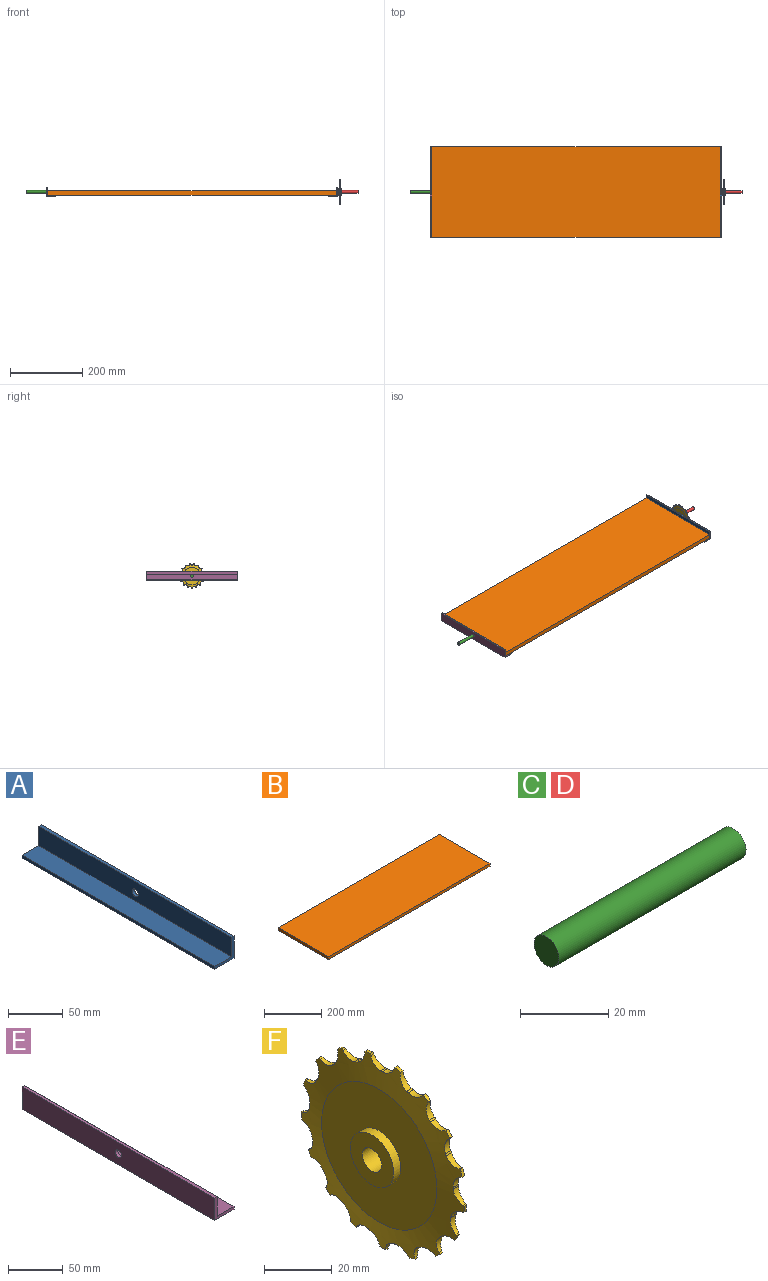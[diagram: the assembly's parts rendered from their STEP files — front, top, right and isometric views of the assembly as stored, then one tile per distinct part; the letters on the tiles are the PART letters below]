
ASSEMBLY  parts=6 mates=5
PART A: 9 faces, bbox 25x250x25 mm
  f0: plane 250x25mm, normal (0,0,-1), area 6250mm2, adj f1,f5,f6,f7
  f1: plane 250x25mm, normal (1,0,0), area 6199.7mm2, adj f0,f2,f6,f7,f8
  f2: plane 250x3.2mm, normal (0,0,1), area 800mm2, adj f1,f3,f6,f7
  f3: plane 250x21.8mm, normal (-1,0,0), area 5399.7mm2, adj f2,f4,f6,f7,f8
  f4: plane 250x21.8mm, normal (0,0,1), area 5450mm2, adj f3,f5,f6,f7
  f5: plane 250x3.2mm, normal (-1,0,0), area 800mm2, adj f0,f4,f6,f7
  f6: plane 25x25mm, normal (0,-1,0), area 149.8mm2, adj f0,f1,f2,f3,f4,f5
  f7: plane 25x25mm, normal (0,1,0), area 149.8mm2, adj f0,f1,f2,f3,f4,f5
  f8: cylinder r=4mm len=8mm, axis (1,0,0), area 80.4mm2, adj f1,f3
PART B: 6 faces, bbox 800x250x12 mm
  f0: plane 800x12mm, normal (0,1,0), area 9600mm2, adj f1,f3,f4,f5
  f1: plane 250x12mm, normal (-1,0,0), area 3000mm2, adj f0,f2,f4,f5
  f2: plane 800x12mm, normal (0,-1,0), area 9600mm2, adj f1,f3,f4,f5
  f3: plane 250x12mm, normal (1,0,0), area 3000mm2, adj f0,f2,f4,f5
  f4: plane 800x250mm, normal (0,0,1), area 200000mm2, adj f0,f1,f2,f3
  f5: plane 800x250mm, normal (0,0,-1), area 200000mm2, adj f0,f1,f2,f3
PART C: 3 faces, bbox 60x8x8 mm
  f0: cylinder r=4mm len=60mm, axis (-1,0,0), area 1508mm2, adj f1,f2
  f1: plane 8x8mm, normal (1,0,0), area 50.3mm2, adj f0
  f2: plane 8x8mm, normal (-1,0,0), area 50.3mm2, adj f0
PART D: same geometry as C
PART E: 11 faces, bbox 25x250x25 mm
  f0: plane 250x21.8mm, normal (0,0,1), area 5410.7mm2, adj f1,f5,f6,f7,f9,f10
  f1: plane 250x21.8mm, normal (1,0,0), area 5399.7mm2, adj f0,f2,f6,f7,f8
  f2: plane 250x3.2mm, normal (0,0,1), area 800mm2, adj f1,f3,f6,f7
  f3: plane 250x25mm, normal (-1,0,0), area 6199.7mm2, adj f2,f4,f6,f7,f8
  f4: plane 250x25mm, normal (0,0,-1), area 6210.7mm2, adj f3,f5,f6,f7,f9,f10
  f5: plane 250x3.2mm, normal (1,0,0), area 800mm2, adj f0,f4,f6,f7
  f6: plane 25x25mm, normal (0,-1,0), area 149.8mm2, adj f0,f1,f2,f3,f4,f5
  f7: plane 25x25mm, normal (0,1,0), area 149.8mm2, adj f0,f1,f2,f3,f4,f5
  f8: cylinder r=4mm len=8mm, axis (1,0,0), area 80.4mm2, adj f1,f3
  f9: cylinder r=2.5mm len=5mm, axis (0,0,1), area 50.3mm2, adj f0,f4
  f10: cylinder r=2.5mm len=5mm, axis (0,0,1), area 50.3mm2, adj f0,f4
PART F: 111 faces, bbox 10x68x68 mm
  f0: cylinder r=34mm len=2.49mm, axis (1,0,0), area 2.5mm2, adj f1,f97,f98,f110
  f1: plane 1.16x0.54mm, normal (0,1,-0.02), area 0.6mm2, adj f0,f2,f97,f98
  f2: cylinder r=4.75mm len=4.54mm, axis (1,0,0), area 10.7mm2, adj f1,f3,f97,f98
  f3: cylinder r=30mm len=2.2mm, axis (1,0,0), area 1.3mm2, adj f2,f4,f97,f98
  f4: cylinder r=4.75mm len=5.34mm, axis (1,0,0), area 10.7mm2, adj f3,f5,f97,f98
  f5: plane 1.16x0.41mm, normal (0,-0.75,0.66), area 0.6mm2, adj f4,f6,f97,f98
  f6: cylinder r=34mm len=2.15mm, axis (1,0,0), area 2.5mm2, adj f5,f7,f97,f98
  f7: plane 1.16x0.5mm, normal (0,0.92,-0.38), area 0.6mm2, adj f6,f8,f97,f98
  f8: cylinder r=4.75mm len=5.35mm, axis (1,0,0), area 10.7mm2, adj f7,f9,f97,f98
  f9: cylinder r=30mm len=2.2mm, axis (1,0,0), area 1.3mm2, adj f8,f10,f97,f98
  f10: cylinder r=4.75mm len=5.44mm, axis (1,0,0), area 10.7mm2, adj f9,f11,f97,f98
  f11: plane 1.16x0.48mm, normal (0,-0.46,0.89), area 0.6mm2, adj f10,f12,f97,f98
  f12: cylinder r=34mm len=2.02mm, axis (1,0,0), area 2.5mm2, adj f11,f13,f97,f98
  f13: plane 1.16x0.39mm, normal (0,0.73,-0.69), area 0.6mm2, adj f12,f14,f97,f98
  f14: cylinder r=4.75mm len=5.43mm, axis (1,0,0), area 10.7mm2, adj f13,f15,f97,f98
  f15: cylinder r=30mm len=2.2mm, axis (1,0,0), area 1.3mm2, adj f14,f16,f97,f98
  f16: cylinder r=4.75mm len=4.81mm, axis (1,0,0), area 10.7mm2, adj f15,f17,f97,f98
  f17: plane 1.16x0.54mm, normal (0,-0.11,0.99), area 0.6mm2, adj f16,f18,f97,f98
  f18: cylinder r=34mm len=2.43mm, axis (1,0,0), area 2.5mm2, adj f17,f19,f97,f98
  f19: plane 1.16x0.49mm, normal (0,0.43,-0.9), area 0.6mm2, adj f18,f20,f97,f98
  f20: cylinder r=4.75mm len=4.78mm, axis (1,0,0), area 10.7mm2, adj f19,f21,f97,f98
  f21: cylinder r=30mm len=2.2mm, axis (1,0,0), area 1.3mm2, adj f20,f22,f97,f98
  f22: cylinder r=4.75mm len=4.2mm, axis (1,0,0), area 10.7mm2, adj f21,f23,f97,f98
  f23: plane 1.16x0.52mm, normal (0,0.25,0.97), area 0.6mm2, adj f22,f24,f97,f98
  f24: cylinder r=34mm len=2.52mm, axis (1,0,0), area 2.5mm2, adj f23,f25,f97,f98
  f25: plane 1.16x0.54mm, normal (0,0.07,-1), area 0.6mm2, adj f24,f26,f97,f98
  f26: cylinder r=4.75mm len=4.24mm, axis (1,0,0), area 10.7mm2, adj f25,f27,f97,f98
  f27: cylinder r=30mm len=2.2mm, axis (1,0,0), area 1.3mm2, adj f26,f28,f97,f98
  f28: cylinder r=4.75mm len=5.19mm, axis (1,0,0), area 10.7mm2, adj f27,f29,f97,f98
  f29: plane 1.16x0.44mm, normal (0,0.59,0.81), area 0.6mm2, adj f28,f30,f97,f98
  f30: cylinder r=34mm len=2.26mm, axis (1,0,0), area 2.5mm2, adj f29,f31,f97,f98
  f31: plane 1.16x0.52mm, normal (0,-0.29,-0.96), area 0.6mm2, adj f30,f32,f97,f98
  f32: cylinder r=4.75mm len=5.21mm, axis (1,0,0), area 10.7mm2, adj f31,f33,f97,f98
  f33: cylinder r=30mm len=2.2mm, axis (1,0,0), area 1.3mm2, adj f32,f34,f97,f98
  f34: cylinder r=4.75mm len=5.48mm, axis (1,0,0), area 10.7mm2, adj f33,f35,f97,f98
  f35: plane 1.16x0.45mm, normal (0,0.84,0.54), area 0.6mm2, adj f34,f36,f97,f98
  f36: cylinder r=34mm len=1.87mm, axis (1,0,0), area 2.5mm2, adj f35,f37,f97,f98
  f37: plane 1.16x0.42mm, normal (0,-0.62,-0.79), area 0.6mm2, adj f36,f38,f97,f98
  f38: cylinder r=4.75mm len=5.48mm, axis (1,0,0), area 10.7mm2, adj f37,f39,f97,f98
  f39: cylinder r=30mm len=2.2mm, axis (1,0,0), area 1.3mm2, adj f38,f40,f97,f98
  f40: cylinder r=4.75mm len=5.03mm, axis (1,0,0), area 10.7mm2, adj f39,f41,f97,f98
  f41: plane 1.16x0.53mm, normal (0,0.98,0.2), area 0.6mm2, adj f40,f42,f97,f98
  f42: cylinder r=34mm len=2.36mm, axis (1,0,0), area 2.5mm2, adj f41,f43,f97,f98
  f43: plane 1.16x0.47mm, normal (0,-0.86,-0.51), area 0.6mm2, adj f42,f44,f97,f98
  f44: cylinder r=4.75mm len=5.01mm, axis (1,0,0), area 10.7mm2, adj f43,f45,f97,f98
  f45: cylinder r=30mm len=2.2mm, axis (1,0,0), area 1.3mm2, adj f44,f46,f97,f98
  f46: cylinder r=4.75mm len=3.9mm, axis (1,0,0), area 10.7mm2, adj f45,f47,f97,f98
  f47: plane 1.16x0.53mm, normal (0,0.99,-0.16), area 0.6mm2, adj f46,f48,f97,f98
  f48: cylinder r=34mm len=2.53mm, axis (1,0,0), area 2.5mm2, adj f47,f49,f97,f98
  f49: plane 1.16x0.53mm, normal (0,-0.99,-0.16), area 0.6mm2, adj f48,f50,f97,f98
  f50: cylinder r=4.75mm len=3.9mm, axis (1,0,0), area 10.7mm2, adj f49,f51,f97,f98
  f51: cylinder r=30mm len=2.2mm, axis (1,0,0), area 1.3mm2, adj f50,f52,f97,f98
  f52: cylinder r=4.75mm len=5.01mm, axis (1,0,0), area 10.7mm2, adj f51,f53,f97,f98
  f53: plane 1.16x0.47mm, normal (0,0.86,-0.51), area 0.6mm2, adj f52,f54,f97,f98
  f54: cylinder r=34mm len=2.36mm, axis (1,0,0), area 2.5mm2, adj f53,f55,f97,f98
  f55: plane 1.16x0.53mm, normal (0,-0.98,0.2), area 0.6mm2, adj f54,f56,f97,f98
  f56: cylinder r=4.75mm len=5.03mm, axis (1,0,0), area 10.7mm2, adj f55,f57,f97,f98
  f57: cylinder r=30mm len=2.2mm, axis (1,0,0), area 1.3mm2, adj f56,f58,f97,f98
  f58: cylinder r=4.75mm len=5.48mm, axis (1,0,0), area 10.7mm2, adj f57,f59,f97,f98
  f59: plane 1.16x0.42mm, normal (0,0.62,-0.79), area 0.6mm2, adj f58,f60,f97,f98
  f60: cylinder r=34mm len=1.87mm, axis (1,0,0), area 2.5mm2, adj f59,f61,f97,f98
  f61: plane 1.16x0.45mm, normal (0,-0.84,0.54), area 0.6mm2, adj f60,f62,f97,f98
  f62: cylinder r=4.75mm len=5.48mm, axis (1,0,0), area 10.7mm2, adj f61,f63,f97,f98
  f63: cylinder r=30mm len=2.2mm, axis (1,0,0), area 1.3mm2, adj f62,f64,f97,f98
  f64: cylinder r=4.75mm len=5.21mm, axis (1,0,0), area 10.7mm2, adj f63,f65,f97,f98
  f65: plane 1.16x0.52mm, normal (0,0.29,-0.96), area 0.6mm2, adj f64,f66,f97,f98
  f66: cylinder r=34mm len=2.26mm, axis (1,0,0), area 2.5mm2, adj f65,f67,f97,f98
  f67: plane 1.16x0.44mm, normal (0,-0.59,0.81), area 0.6mm2, adj f66,f68,f97,f98
  f68: cylinder r=4.75mm len=5.19mm, axis (1,0,0), area 10.7mm2, adj f67,f69,f97,f98
  f69: cylinder r=30mm len=2.2mm, axis (1,0,0), area 1.3mm2, adj f68,f70,f97,f98
  f70: cylinder r=4.75mm len=4.24mm, axis (1,0,0), area 10.7mm2, adj f69,f71,f97,f98
  f71: plane 1.16x0.54mm, normal (0,-0.07,-1), area 0.6mm2, adj f70,f72,f97,f98
  f72: cylinder r=34mm len=2.52mm, axis (1,0,0), area 2.5mm2, adj f71,f73,f97,f98
  f73: plane 1.16x0.52mm, normal (0,-0.25,0.97), area 0.6mm2, adj f72,f74,f97,f98
  f74: cylinder r=4.75mm len=4.2mm, axis (1,0,0), area 10.7mm2, adj f73,f75,f97,f98
  f75: cylinder r=30mm len=2.2mm, axis (1,0,0), area 1.3mm2, adj f74,f76,f97,f98
  f76: cylinder r=4.75mm len=4.78mm, axis (1,0,0), area 10.7mm2, adj f75,f77,f97,f98
  f77: plane 1.16x0.49mm, normal (0,-0.43,-0.9), area 0.6mm2, adj f76,f78,f97,f98
  f78: cylinder r=34mm len=2.43mm, axis (1,0,0), area 2.5mm2, adj f77,f79,f97,f98
  f79: plane 1.16x0.54mm, normal (0,0.11,0.99), area 0.6mm2, adj f78,f80,f97,f98
  f80: cylinder r=4.75mm len=4.81mm, axis (1,0,0), area 10.7mm2, adj f79,f81,f97,f98
  f81: cylinder r=30mm len=2.2mm, axis (1,0,0), area 1.3mm2, adj f80,f82,f97,f98
  f82: cylinder r=4.75mm len=5.43mm, axis (1,0,0), area 10.7mm2, adj f81,f83,f97,f98
  f83: plane 1.16x0.39mm, normal (0,-0.73,-0.69), area 0.6mm2, adj f82,f84,f97,f98
  f84: cylinder r=34mm len=2.02mm, axis (1,0,0), area 2.5mm2, adj f83,f85,f97,f98
  f85: plane 1.16x0.48mm, normal (0,0.46,0.89), area 0.6mm2, adj f84,f86,f97,f98
  f86: cylinder r=4.75mm len=5.44mm, axis (1,0,0), area 10.7mm2, adj f85,f87,f97,f98
  f87: cylinder r=30mm len=2.2mm, axis (1,0,0), area 1.3mm2, adj f86,f88,f97,f98
  f88: cylinder r=4.75mm len=5.35mm, axis (1,0,0), area 10.7mm2, adj f87,f89,f97,f98
  f89: plane 1.16x0.5mm, normal (0,-0.92,-0.38), area 0.6mm2, adj f88,f90,f97,f98
  f90: cylinder r=34mm len=2.15mm, axis (1,0,0), area 2.5mm2, adj f89,f91,f97,f98
  f91: plane 1.16x0.41mm, normal (0,0.75,0.66), area 0.6mm2, adj f90,f92,f97,f98
  f92: cylinder r=4.75mm len=5.34mm, axis (1,0,0), area 10.7mm2, adj f91,f93,f97,f98
  f93: cylinder r=30mm len=2.2mm, axis (1,0,0), area 1.3mm2, adj f92,f94,f97,f98
  f94: cylinder r=4.75mm len=4.54mm, axis (1,0,0), area 10.7mm2, adj f93,f95,f97,f98
  f95: plane 1.16x0.54mm, normal (0,-1,-0.02), area 0.6mm2, adj f94,f96,f97,f98
  f96: cylinder r=34mm len=2.49mm, axis (1,0,0), area 2.5mm2, adj f95,f97,f98,f106
  f97: cone r=24mm half-angle=81.5deg, axis (-1,0,0), area 1327.6mm2, adj f0,f1,f2,f3,f4,f5,f6,f7
  f98: cone r=24mm half-angle=81.5deg, axis (1,0,0), area 1327.6mm2, adj f0,f1,f2,f3,f4,f5,f6,f7
  f99: cylinder r=4mm len=10mm, axis (1,0,0), area 251.3mm2, adj f100,f105
  f100: plane 18x18mm, normal (1,0,0), area 204.2mm2, adj f99,f101
  f101: cylinder r=9mm len=18mm, axis (1,0,0), area 169.6mm2, adj f100,f102
  f102: plane 48x48mm, normal (1,0,0), area 1555.1mm2, adj f97,f101
  f103: plane 48x48mm, normal (-1,0,0), area 1555.1mm2, adj f98,f104
  f104: cylinder r=9mm len=18mm, axis (1,0,0), area 169.6mm2, adj f103,f105
  f105: plane 18x18mm, normal (-1,0,0), area 204.2mm2, adj f99,f104
  f106: plane 1.16x0.51mm, normal (0,0.94,0.34), area 0.6mm2, adj f96,f97,f98,f107
  f107: cylinder r=4.75mm len=4.51mm, axis (1,0,0), area 10.7mm2, adj f97,f98,f106,f108
  f108: cylinder r=30mm len=2.2mm, axis (1,0,0), area 1.3mm2, adj f97,f98,f107,f109
  f109: cylinder r=4.75mm len=4.51mm, axis (1,0,0), area 10.7mm2, adj f97,f98,f108,f110
  f110: plane 1.16x0.51mm, normal (0,-0.94,0.34), area 0.6mm2, adj f0,f97,f98,f109
PLACE A t=(397.68,-2.33,-8.01)mm
PLACE B t=(-5.52,-2.33,1.29)mm
PLACE C t=(-435.52,-2.33,4.49)mm
PLACE D t=(424.48,-2.33,4.49)mm
PLACE E t=(-405.52,-2.33,-4.81)mm
PLACE F t=(404.48,-2.33,4.49)mm
MATE fastened C.f0 <-> B.f1  axis (1,0,0) through (-405.52,-2.33,4.49)mm
MATE fastened F.f0 <-> D.f0  axis (-1,0,0) through (399.48,-2.33,4.49)mm
MATE fastened D.f0 <-> A.f8  axis (-1,0,0) through (394.48,-2.33,4.49)mm
MATE fastened D.f0 <-> B.f3  axis (-1,0,0) through (394.48,-2.33,4.49)mm
MATE fastened C.f0 <-> E.f8  axis (-1,0,0) through (-405.52,-2.33,4.49)mm
